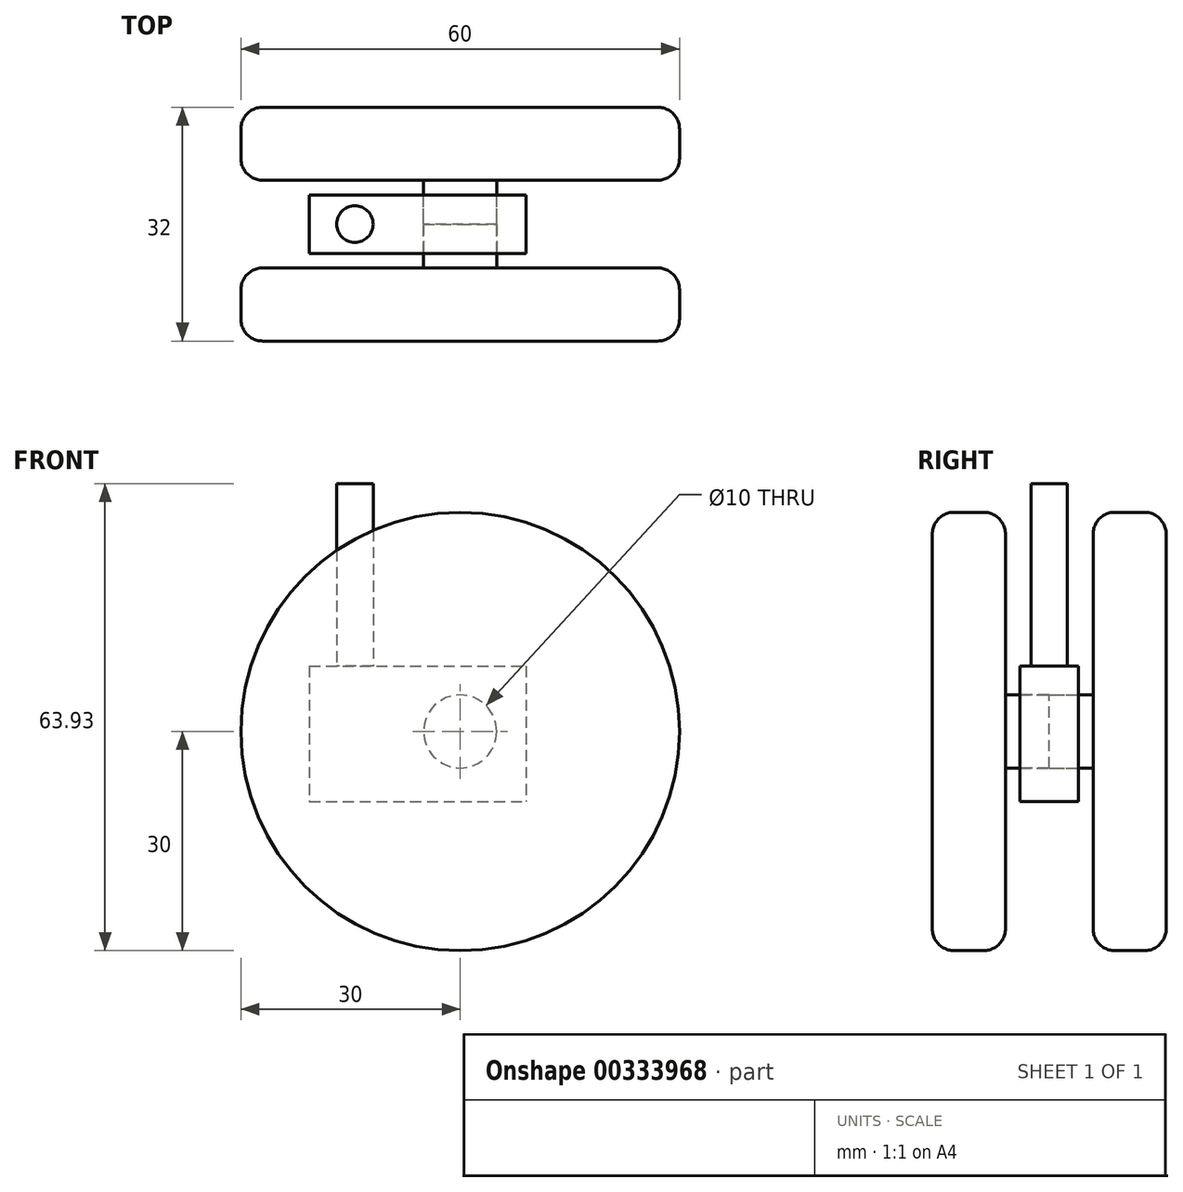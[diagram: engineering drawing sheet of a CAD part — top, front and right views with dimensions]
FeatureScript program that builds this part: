
annotation { "Feature Type Name" : "Feature", "Feature Type Description" : "" }
export const myFeature = defineFeature(function(context is Context, id is Id, definition is map)
    precondition{}
    {
        {
            var Q0;
            Q0=qCreatedBy(makeId("Front.planeOp"),FACE);
            var sketch = newSketch(context, id + "F0", { "sketchPlane" : qUnion([Q0])});
            skCircle(sketch, "E0", {"center": v(0, 0) * mm, "radius": 30 * mm});
            skSolve(sketch);
        }
        {
            var Q0;
            Q0 = qSketchRegion(id + "F0", true);
            extrude(context, id + "F1", {"entities" : qUnion([Q0]), "depth" : 10 * mm});
        }
        {
            var Q0;
            Q0=makeQuery(id+"F1.opExtrude","CAP_EDGE",EDGE,{"disambiguationData":[OSD([sQuery(id+"F0.wireOp",EDGE,"E0")])],"isStart":false});
            fillet(context, id + "F2", {"entities" : qUnion([Q0]), "radius" : 3 * mm, "tangentPropagation" : true, "allowEdgeOverflow" : false});
        }
        {
            var Q0;
            Q0=makeQuery(id+"F1.opExtrude","CAP_EDGE",EDGE,{"disambiguationData":[OSD([sQuery(id+"F0.wireOp",EDGE,"E0")])],"isStart":true});
            fillet(context, id + "F3", {"entities" : qUnion([Q0]), "radius" : 3 * mm, "tangentPropagation" : true, "allowEdgeOverflow" : false});
        }
        {
            var Q0;
            Q0=makeQuery(id+"F1.opExtrude","CAP_FACE",FACE,{"disambiguationData":[OSD([sQuery(id+"F0.wireOp",EDGE,"E0")])],"isStart":false});
            var sketch = newSketch(context, id + "F4", { "sketchPlane" : qUnion([Q0])});
            skCircle(sketch, "E1", {"center": v(0, 0) * mm, "radius": 5 * mm});
            skSolve(sketch);
        }
        {
            var Q0;
            Q0 = qSketchRegion(id + "F4", true);
            extrude(context, id + "F5", {"entities" : qUnion([Q0]), "operationType" : NewBodyOperationType.ADD, "depth" : 6 * mm});
        }
        {
            var Q0;
            Q0=makeQuery(id+"F1.opExtrude","SWEPT_BODY",BODY,{"disambiguationData":[OSD([sQuery(id+"F0.wireOp",EDGE,"E0")])]});
            var Q1;
            Q1=makeQuery(id+"F5.opExtrude","CAP_FACE",FACE,{"disambiguationData":[OSD([sQuery(id+"F4.wireOp",EDGE,"E1")])],"isStart":false});
            mirror(context, id + "F6", {"entities" : qUnion([Q0]), "mirrorPlane" : qUnion([Q1])});
        }
        {
            var Q0;
            Q0=makeQuery(id+"F5.opExtrude","CAP_FACE",FACE,{"disambiguationData":[OSD([sQuery(id+"F4.wireOp",EDGE,"E1")])],"isStart":false});
            var sketch = newSketch(context, id + "F7", { "sketchPlane" : qUnion([Q0])});
            skLineSegment(sketch, "E2.bottom", {"start": v(-20.65, 8.93) * mm, "end": v(9.03, 8.93) * mm});
            skLineSegment(sketch, "E2.top", {"start": v(-20.65, -9.57) * mm, "end": v(9.03, -9.57) * mm});
            skLineSegment(sketch, "E2.left", {"start": v(-20.65, 8.93) * mm, "end": v(-20.65, -9.57) * mm});
            skLineSegment(sketch, "E2.right", {"start": v(9.03, 8.93) * mm, "end": v(9.03, -9.57) * mm});
            skSolve(sketch);
        }
        {
            var Q0;
            Q0=makeQuery(id+"F7.imprint","IMPRINT",FACE,{"disambiguationData":[TD([[makeQuery(id+"F7.imprint","IMPRINT",EDGE,{"derivedFrom":sQuery(id+"F7.wireOp",EDGE,"E2.bottom")}),-1.0]])]});
            extrude(context, id + "F8", {"entities" : qUnion([Q0]), "endBound" : BoundingType.SYMMETRIC, "depth" : 8 * mm});
        }
        {
            var Q0;
            Q0=makeQuery(id+"F8.opExtrude","SWEPT_FACE",FACE,{"disambiguationData":[OSD([sQuery(id+"F7.wireOp",EDGE,"E2.bottom")])]});
            var sketch = newSketch(context, id + "F9", { "sketchPlane" : qUnion([Q0])});
            skCircle(sketch, "E3", {"center": v(-14.41, -16) * mm, "radius": 2.5 * mm});
            skPoint(sketch, "E3.centerSnap0", {"position": v(-20.65, -16) * mm});
            skSolve(sketch);
        }
        {
            var Q0;
            Q0=makeQuery(id+"F9.imprint","IMPRINT",FACE,{"disambiguationData":[TD([[makeQuery(id+"F9.imprint","IMPRINT",EDGE,{"derivedFrom":sQuery(id+"F9.wireOp",EDGE,"E3")}),1.0]])]});
            extrude(context, id + "F10", {"entities" : qUnion([Q0]), "operationType" : NewBodyOperationType.ADD, "depth" : 25 * mm});
        }
    });
